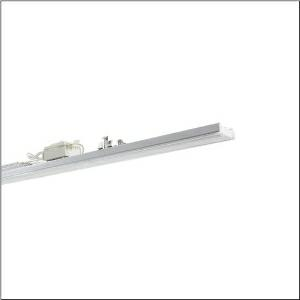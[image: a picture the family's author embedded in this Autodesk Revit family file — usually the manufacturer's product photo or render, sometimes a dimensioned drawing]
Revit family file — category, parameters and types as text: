
# Revit family: licross_11_recessed_mo_51tl19mn495g
name_source: partatom
category: Lighting Fixtures
units: mm (PartAtom-declared; Revit-internal decimal feet)

## family parameters
Cut with Voids When Loaded = No
Host = Face
Light Source = No
Part Type = Normal
Room Calculation Point = No
Round Connector Dimension = Use Diameter
Shared = No

## types (1)
- --- (1 x LED, 9850 lm, 55.2 W, 4000K)
    Apparent Load = 55 VA
    CIE Flux Codes = 55 90 98 100 100
    Color Rendering = 80
    Color Temperature = 4000K
    Default Elevation = 1800 mm
    Description = Licross 11 Recessed MO, luminaire insert, of sheet steel, coil coated, white, length: 1.500mm, width: 66mm, height: 67mm, LED rated luminous flux: 9.860lm, light colour: 840, SDCM (Standard Deviation of Colour Matching)MacAdam ≤ 2 SDCM (initial), control gear: ON/OFF Multilumen, with plug, 3-pole, with phase selection, mains connection: 220..240V, AC, 50/60Hz, rated input power: 55W, internal wiring halogen-free, primary light control with lens, of plastic, primary optical cover: cover, of PMMA, light emission: direct distribution, primary light characteristic: double asymmetric, protection rating (complete): IP40, insulation class (complete): insulation class I (protective earthing), certification: CE, ENEC, VDE, UKCA, protection symbol: D if used in an environment without relevant dust loads with corresponding accessories, impact resistance: IK06, permissible ambient temperature for indoor applications: -35..+40°C, corresponds to IFS (International Featured Standards) requirements for safety and quality in the food industry, reducing of maximum allowable ambient temperature of 5°C with ceiling mounting, The light source and the operating device comply with the requirements of the Ecodesign Regulation (EU) 2019/2020 and are replaceable in accordance with this regulation, packaging unit: 1 piece
    Height = 58 mm
    Lamp = 1 x LED
    Lamp Light Flux = 9850 lm
    Lamp Power = 55.2 W
    Lamp count = 1
    Length = 1500 mm
    Luminous efficacy = 178 lm/W
    Manufacturer = Siteco
    ModVariant = No
    Model = 51TL19MN495G
    Mounting Place = Ceiling
    Mounting Type = Pendant
    Number of Poles = 1
    OnlyDefault = Yes
    Power Factor = 1
    Product Name = Licross 11 Recessed MO
    Product group = luminaire insert | ceiling pendant
    ProductGroupID = 901
    Protection Class = Protection class I
    Protection Degree = IP 40
    RLX_Detail_Level = 1
    RLX_Emergency_Light_Flux = 0 lm
    RLX_Emergency_Type = 0
    RLX_Emergency_Type_DB = No
    RlxData = <blob elided: 22453 chars, md5=32866466>
    Socket = socket
    Standby Power = 0 W
    System Light Flux = 9850 lm
    System Power = 55 W
    Type Comments = factory setting: luminous flux: 100 % | (A | C | E) | 126 mA
    Type Image = l_1296930.jpg
    URL = http://relux.com
    VarID = @adj_090337
    Voltage = 0 V
    Weight = 0.00 kg
    Width = 66 mm

## geometry (parser evidence)
native form markers: Blend x4, Sweep x12
no freeform markers — native parametric forms only
